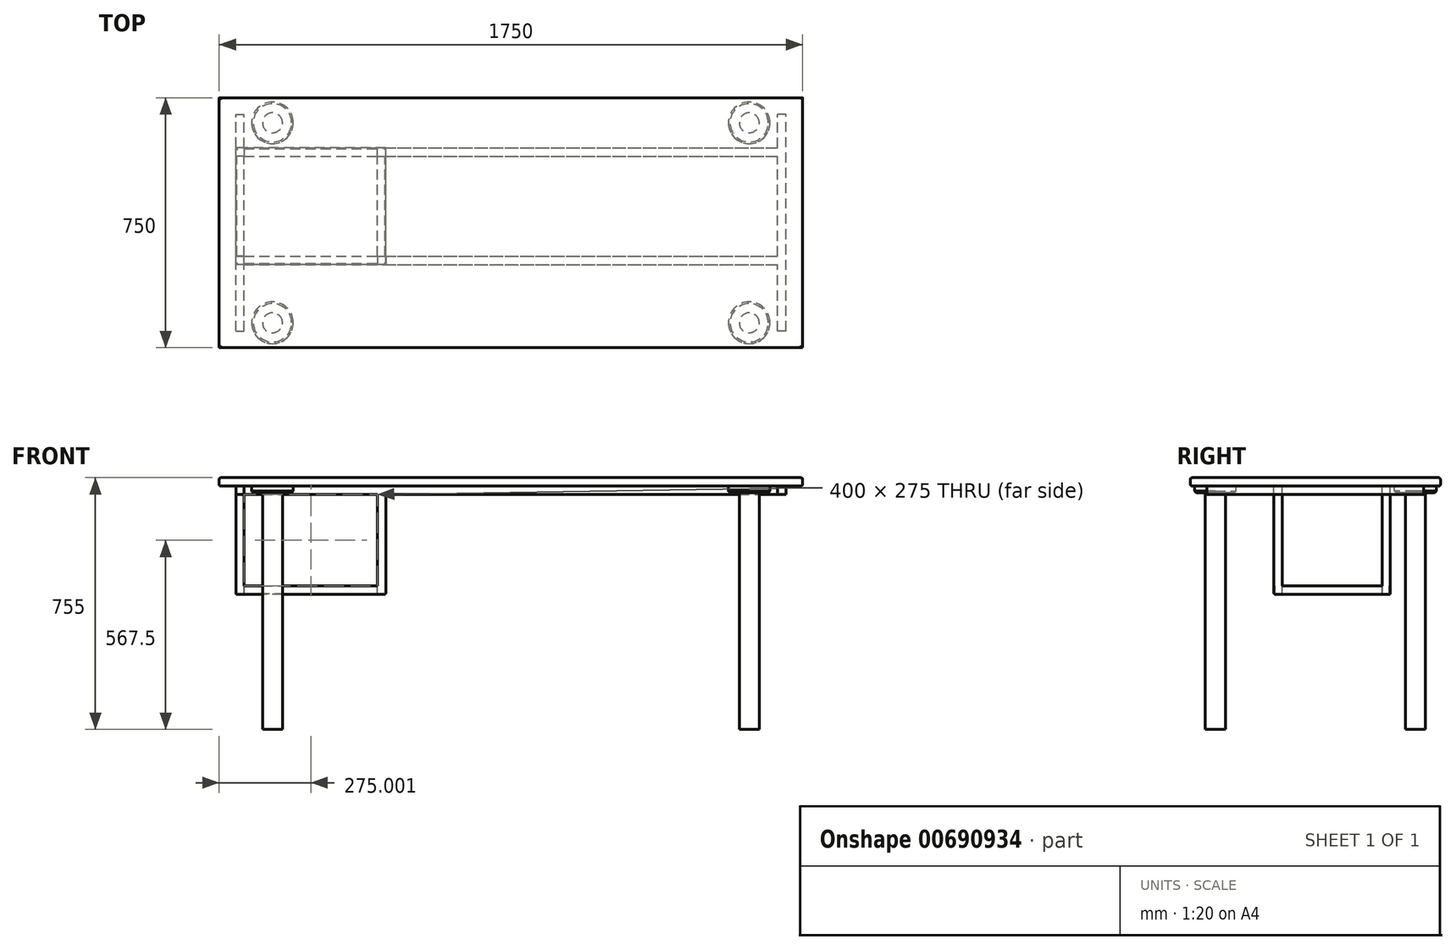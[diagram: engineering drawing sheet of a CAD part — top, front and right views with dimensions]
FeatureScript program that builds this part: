
annotation { "Feature Type Name" : "Feature", "Feature Type Description" : "" }
export const myFeature = defineFeature(function(context is Context, id is Id, definition is map)
    precondition{}
    {
        {
            var Q0;
            Q0=qCreatedBy(makeId("Top.planeOp"),FACE);
            var sketch = newSketch(context, id + "F0", { "sketchPlane" : qUnion([Q0])});
            skLineSegment(sketch, "E0.bottom", {"start": v(-773.1, 399.75) * mm, "end": v(976.9, 399.75) * mm});
            skLineSegment(sketch, "E0.top", {"start": v(-773.1, -350.25) * mm, "end": v(976.9, -350.25) * mm});
            skLineSegment(sketch, "E0.left", {"start": v(-773.1, 399.75) * mm, "end": v(-773.1, -350.25) * mm});
            skLineSegment(sketch, "E0.right", {"start": v(976.9, 399.75) * mm, "end": v(976.9, -350.25) * mm});
            skSolve(sketch);
        }
        {
            var Q0;
            Q0=makeQuery(id+"F0.imprint","IMPRINT",FACE,{"disambiguationData":[TD([[makeQuery(id+"F0.imprint","IMPRINT",EDGE,{"derivedFrom":sQuery(id+"F0.wireOp",EDGE,"E0.bottom")}),-1.0]])]});
            extrude(context, id + "F1", {"entities" : qUnion([Q0]), "depth" : 25 * mm, "offsetDistance" : 25 * mm});
        }
        {
            var Q0;
            Q0=makeQuery(id+"F1.opExtrude","CAP_FACE",FACE,{"disambiguationData":[OSD([sQuery(id+"F0.wireOp",EDGE,"E0.bottom"),sQuery(id+"F0.wireOp",EDGE,"E0.top"),sQuery(id+"F0.wireOp",EDGE,"E0.left"),sQuery(id+"F0.wireOp",EDGE,"E0.right")])],"isStart":true});
            var sketch = newSketch(context, id + "F2", { "sketchPlane" : qUnion([Q0])});
            skLineSegment(sketch, "E1.bottom", {"start": v(-723.1, 300.25) * mm, "end": v(-698.1, 300.25) * mm});
            skLineSegment(sketch, "E1.top", {"start": v(-723.1, -349.75) * mm, "end": v(-698.1, -349.75) * mm});
            skLineSegment(sketch, "E1.left", {"start": v(-723.1, 300.25) * mm, "end": v(-723.1, -349.75) * mm});
            skPoint(sketch, "E1.middle", {"position": v(-710.6, -24.75) * mm});
            skPoint(sketch, "E1.middle.positionSnap0", {"position": v(-773.1, -24.75) * mm});
            skPoint(sketch, "E1.centerSnap0", {"position": v(-773.1, -24.75) * mm});
            skLineSegment(sketch, "E2", {"start": v(101.9, 350.25) * mm, "end": v(101.9, -399.75) * mm, "construction": true});
            skLineSegment(sketch, "E3.MirrorCS", {"start": v(926.9, 300.25) * mm, "end": v(901.9, 300.25) * mm});
            skLineSegment(sketch, "E4.MirrorCS", {"start": v(926.9, 300.25) * mm, "end": v(926.9, -349.75) * mm});
            skLineSegment(sketch, "E5.MirrorCS", {"start": v(926.9, -349.75) * mm, "end": v(901.9, -349.75) * mm});
            skLineSegment(sketch, "E6.left", {"start": v(-723.1, -349.75) * mm, "end": v(-723.1, -324.75) * mm});
            skLineSegment(sketch, "E6.right", {"start": v(926.9, -349.75) * mm, "end": v(926.9, -324.75) * mm});
            skPoint(sketch, "E7.middle", {"position": v(101.9, -24.75) * mm});
            skPoint(sketch, "E8.orphan", {"position": v(901.9, -349.75) * mm});
            skLineSegment(sketch, "E9.trimOffspring", {"start": v(901.9, -349.75) * mm, "end": v(926.9, -349.75) * mm});
            skPoint(sketch, "E10.trimOffspring.start.orphan", {"position": v(-698.1, -37.25) * mm});
            skPoint(sketch, "E1.right.end.orphan", {"position": v(-698.1, -12.25) * mm});
            skPoint(sketch, "E11.MirrorCS.end.orphan", {"position": v(901.9, -12.25) * mm});
            skPoint(sketch, "E11.MirrorCS.start.orphan", {"position": v(901.9, 300.25) * mm});
            skPoint(sketch, "E12.trimOffspring.start.orphan", {"position": v(901.9, -37.25) * mm});
            skLineSegment(sketch, "E13", {"start": v(901.9, 300.25) * mm, "end": v(901.9, 100.25) * mm});
            skLineSegment(sketch, "E14", {"start": v(-698.1, 300.25) * mm, "end": v(-698.1, 100.25) * mm});
            skLineSegment(sketch, "E15.bottom", {"start": v(-698.1, -249.75) * mm, "end": v(901.9, -249.75) * mm});
            skLineSegment(sketch, "E15.top", {"start": v(-698.1, -224.75) * mm, "end": v(901.9, -224.75) * mm});
            skLineSegment(sketch, "E16.bottom", {"start": v(-698.1, 75.25) * mm, "end": v(901.9, 75.25) * mm});
            skLineSegment(sketch, "E16.top", {"start": v(-698.1, 100.25) * mm, "end": v(901.9, 100.25) * mm});
            skLineSegment(sketch, "E17.trimOffspring", {"start": v(-698.1, 75.25) * mm, "end": v(-698.1, -224.75) * mm});
            skLineSegment(sketch, "E18.trimOffspring", {"start": v(-698.1, -249.75) * mm, "end": v(-698.1, -349.75) * mm});
            skLineSegment(sketch, "E19.trimOffspring", {"start": v(901.9, -249.75) * mm, "end": v(901.9, -349.75) * mm});
            skLineSegment(sketch, "E20.trimOffspring", {"start": v(901.9, 75.25) * mm, "end": v(901.9, -224.75) * mm});
            skSolve(sketch);
        }
        {
            var Q0;
            Q0=makeQuery(id+"F2.imprint","IMPRINT",FACE,{"disambiguationData":[TD([[makeQuery(id+"F2.imprint","IMPRINT",EDGE,{"derivedFrom":sQuery(id+"F2.wireOp",EDGE,"E1.bottom")}),-1.0]])]});
            extrude(context, id + "F3", {"entities" : qUnion([Q0]), "operationType" : NewBodyOperationType.ADD, "depth" : 25 * mm, "offsetDistance" : 25 * mm});
        }
        {
            var Q0;
            {var subQ0=sQuery(id+"F0.wireOp",EDGE,"E0.left");var subQ1=sQuery(id+"F0.wireOp",EDGE,"E0.bottom");var subQ2=sQuery(id+"F0.wireOp",EDGE,"E0.right");var subQ3=sQuery(id+"F0.wireOp",EDGE,"E0.top");Q0=makeQuery(id+"F3.boolean.opBoolean","SPLIT",FACE,{"disambiguationData":[TD([makeQuery(id+"F1.opExtrude","SWEPT_FACE",FACE,{"disambiguationData":[OSD([subQ1])]})])],"derivedFrom":makeQuery(id+"F1.opExtrude","CAP_FACE",FACE,{"disambiguationData":[OSD([subQ1,subQ3,subQ0,subQ2])],"isStart":true})});}
            var sketch = newSketch(context, id + "F4", { "sketchPlane" : qUnion([Q0])});
            skLineSegment(sketch, "E21", {"start": v(-572.48, -324.75) * mm, "end": v(-698.1, -324.75) * mm, "construction": true});
            skLineSegment(sketch, "E22", {"start": v(-572.48, -324.75) * mm, "end": v(901.9, -324.75) * mm, "construction": true});
            skCircle(sketch, "E23", {"center": v(-613.1, -324.75) * mm, "radius": 62.5 * mm});
            skLineSegment(sketch, "E24", {"start": v(101.9, 350.25) * mm, "end": v(101.9, -399.75) * mm, "construction": true});
            skCircle(sketch, "E25", {"center": v(816.9, -324.75) * mm, "radius": 62.5 * mm});
            skCircle(sketch, "E26", {"center": v(-613.1, 275.25) * mm, "radius": 62.5 * mm});
            skCircle(sketch, "E27", {"center": v(816.9, 275.25) * mm, "radius": 62.5 * mm});
            skCircle(sketch, "E28", {"center": v(-613.1, 275.25) * mm, "radius": 30 * mm});
            skCircle(sketch, "E29", {"center": v(-613.1, -324.75) * mm, "radius": 30 * mm});
            skCircle(sketch, "E30", {"center": v(816.9, -324.75) * mm, "radius": 30 * mm});
            skCircle(sketch, "E31", {"center": v(816.9, 275.25) * mm, "radius": 30 * mm});
            skSolve(sketch);
        }
        {
            var Q0;
            Q0=makeQuery(id+"F4.imprint","IMPRINT",FACE,{"disambiguationData":[TD([[makeQuery(id+"F4.imprint","IMPRINT",EDGE,{"derivedFrom":sQuery(id+"F4.wireOp",EDGE,"E27")}),1.0]])]});
            var Q1;
            Q1=makeQuery(id+"F4.imprint","IMPRINT",FACE,{"disambiguationData":[TD([[makeQuery(id+"F4.imprint","IMPRINT",EDGE,{"derivedFrom":sQuery(id+"F4.wireOp",EDGE,"E26")}),1.0]])]});
            var Q2;
            Q2=makeQuery(id+"F4.imprint","IMPRINT",FACE,{"disambiguationData":[TD([[makeQuery(id+"F4.imprint","IMPRINT",EDGE,{"derivedFrom":sQuery(id+"F4.wireOp",EDGE,"E23")}),1.0]])]});
            var Q3;
            Q3=makeQuery(id+"F4.imprint","IMPRINT",FACE,{"disambiguationData":[TD([[makeQuery(id+"F4.imprint","IMPRINT",EDGE,{"derivedFrom":sQuery(id+"F4.wireOp",EDGE,"E25")}),1.0]])]});
            extrude(context, id + "F5", {"entities" : qUnion([Q0, Q1, Q2, Q3]), "operationType" : NewBodyOperationType.ADD, "depth" : 20 * mm, "offsetDistance" : 25 * mm});
        }
        {
            var Q0;
            {var subQ0=sQuery(id+"F0.wireOp",EDGE,"E0.left");var subQ1=sQuery(id+"F0.wireOp",EDGE,"E0.bottom");var subQ2=sQuery(id+"F0.wireOp",EDGE,"E0.right");var subQ3=sQuery(id+"F0.wireOp",EDGE,"E0.top");Q0=makeQuery(id+"F5.boolean.opBoolean","SPLIT",FACE,{"disambiguationData":[TD([makeQuery(id+"F5.opExtrude","SWEPT_FACE",FACE,{"disambiguationData":[OSD([sQuery(id+"F4.wireOp",EDGE,"E30")])]})])],"derivedFrom":makeQuery(id+"F3.boolean.opBoolean","SPLIT",FACE,{"disambiguationData":[TD([makeQuery(id+"F1.opExtrude","SWEPT_FACE",FACE,{"disambiguationData":[OSD([subQ1])]})])],"derivedFrom":makeQuery(id+"F1.opExtrude","CAP_FACE",FACE,{"disambiguationData":[OSD([subQ1,subQ3,subQ0,subQ2])],"isStart":true})})});}
            var Q1;
            {var subQ0=sQuery(id+"F0.wireOp",EDGE,"E0.left");var subQ1=sQuery(id+"F0.wireOp",EDGE,"E0.bottom");var subQ2=sQuery(id+"F0.wireOp",EDGE,"E0.right");var subQ3=sQuery(id+"F0.wireOp",EDGE,"E0.top");Q1=makeQuery(id+"F5.boolean.opBoolean","SPLIT",FACE,{"disambiguationData":[TD([makeQuery(id+"F5.opExtrude","SWEPT_FACE",FACE,{"disambiguationData":[OSD([sQuery(id+"F4.wireOp",EDGE,"E29")])]})])],"derivedFrom":makeQuery(id+"F3.boolean.opBoolean","SPLIT",FACE,{"disambiguationData":[TD([makeQuery(id+"F1.opExtrude","SWEPT_FACE",FACE,{"disambiguationData":[OSD([subQ1])]})])],"derivedFrom":makeQuery(id+"F1.opExtrude","CAP_FACE",FACE,{"disambiguationData":[OSD([subQ1,subQ3,subQ0,subQ2])],"isStart":true})})});}
            var Q2;
            {var subQ0=sQuery(id+"F0.wireOp",EDGE,"E0.left");var subQ1=sQuery(id+"F0.wireOp",EDGE,"E0.bottom");var subQ2=sQuery(id+"F0.wireOp",EDGE,"E0.right");var subQ3=sQuery(id+"F0.wireOp",EDGE,"E0.top");Q2=makeQuery(id+"F5.boolean.opBoolean","SPLIT",FACE,{"disambiguationData":[TD([makeQuery(id+"F5.opExtrude","SWEPT_FACE",FACE,{"disambiguationData":[OSD([sQuery(id+"F4.wireOp",EDGE,"E28")])]})])],"derivedFrom":makeQuery(id+"F3.boolean.opBoolean","SPLIT",FACE,{"disambiguationData":[TD([makeQuery(id+"F1.opExtrude","SWEPT_FACE",FACE,{"disambiguationData":[OSD([subQ1])]})])],"derivedFrom":makeQuery(id+"F1.opExtrude","CAP_FACE",FACE,{"disambiguationData":[OSD([subQ1,subQ3,subQ0,subQ2])],"isStart":true})})});}
            var Q3;
            {var subQ0=sQuery(id+"F0.wireOp",EDGE,"E0.left");var subQ1=sQuery(id+"F0.wireOp",EDGE,"E0.bottom");var subQ2=sQuery(id+"F0.wireOp",EDGE,"E0.right");var subQ3=sQuery(id+"F0.wireOp",EDGE,"E0.top");Q3=makeQuery(id+"F5.boolean.opBoolean","SPLIT",FACE,{"disambiguationData":[TD([makeQuery(id+"F5.opExtrude","SWEPT_FACE",FACE,{"disambiguationData":[OSD([sQuery(id+"F4.wireOp",EDGE,"E31")])]})])],"derivedFrom":makeQuery(id+"F3.boolean.opBoolean","SPLIT",FACE,{"disambiguationData":[TD([makeQuery(id+"F1.opExtrude","SWEPT_FACE",FACE,{"disambiguationData":[OSD([subQ1])]})])],"derivedFrom":makeQuery(id+"F1.opExtrude","CAP_FACE",FACE,{"disambiguationData":[OSD([subQ1,subQ3,subQ0,subQ2])],"isStart":true})})});}
            extrude(context, id + "F6", {"entities" : qUnion([Q0, Q1, Q2, Q3]), "operationType" : NewBodyOperationType.ADD, "depth" : 730 * mm, "offsetDistance" : 25 * mm});
        }
        {
            var Q0;
            Q0=makeQuery(id+"F3.opExtrude","CAP_FACE",FACE,{"disambiguationData":[OSD([sQuery(id+"F2.wireOp",EDGE,"E1.bottom"),sQuery(id+"F2.wireOp",EDGE,"E1.left"),sQuery(id+"F2.wireOp",EDGE,"E3.MirrorCS"),sQuery(id+"F2.wireOp",EDGE,"E4.MirrorCS"),sQuery(id+"F2.wireOp",EDGE,"E1.top"),sQuery(id+"F2.wireOp",EDGE,"E6.left"),sQuery(id+"F2.wireOp",EDGE,"E6.right"),sQuery(id+"F2.wireOp",EDGE,"E9.trimOffspring"),sQuery(id+"F2.wireOp",EDGE,"E13"),sQuery(id+"F2.wireOp",EDGE,"E14"),sQuery(id+"F2.wireOp",EDGE,"E15.bottom"),sQuery(id+"F2.wireOp",EDGE,"E15.top"),sQuery(id+"F2.wireOp",EDGE,"E16.bottom"),sQuery(id+"F2.wireOp",EDGE,"E16.top"),sQuery(id+"F2.wireOp",EDGE,"E17.trimOffspring"),sQuery(id+"F2.wireOp",EDGE,"E18.trimOffspring"),sQuery(id+"F2.wireOp",EDGE,"E19.trimOffspring"),sQuery(id+"F2.wireOp",EDGE,"E20.trimOffspring")])],"isStart":false});
            var sketch = newSketch(context, id + "F7", { "sketchPlane" : qUnion([Q0])});
            skLineSegment(sketch, "E32.bottom", {"start": v(-698.1, 100.25) * mm, "end": v(-723.1, 100.25) * mm});
            skLineSegment(sketch, "E32.top", {"start": v(-698.1, 75.25) * mm, "end": v(-723.1, 75.25) * mm});
            skLineSegment(sketch, "E32.left", {"start": v(-698.1, 100.25) * mm, "end": v(-698.1, 75.25) * mm});
            skLineSegment(sketch, "E32.right", {"start": v(-723.1, 100.25) * mm, "end": v(-723.1, 75.25) * mm});
            skLineSegment(sketch, "E33.bottom", {"start": v(-698.1, -249.75) * mm, "end": v(-723.1, -249.75) * mm});
            skLineSegment(sketch, "E33.top", {"start": v(-698.1, -224.75) * mm, "end": v(-723.1, -224.75) * mm});
            skLineSegment(sketch, "E33.left", {"start": v(-698.1, -249.75) * mm, "end": v(-698.1, -224.75) * mm});
            skLineSegment(sketch, "E33.right", {"start": v(-723.1, -249.75) * mm, "end": v(-723.1, -224.75) * mm});
            skLineSegment(sketch, "E34.bottom", {"start": v(-298.1, -224.75) * mm, "end": v(-273.1, -224.75) * mm});
            skLineSegment(sketch, "E34.top", {"start": v(-298.1, -249.75) * mm, "end": v(-273.1, -249.75) * mm});
            skLineSegment(sketch, "E34.left", {"start": v(-298.1, -224.75) * mm, "end": v(-298.1, -249.75) * mm});
            skLineSegment(sketch, "E34.right", {"start": v(-273.1, -224.75) * mm, "end": v(-273.1, -249.75) * mm});
            skLineSegment(sketch, "E35.bottom", {"start": v(-273.1, 75.25) * mm, "end": v(-298.1, 75.25) * mm});
            skLineSegment(sketch, "E35.top", {"start": v(-273.1, 100.25) * mm, "end": v(-298.1, 100.25) * mm});
            skLineSegment(sketch, "E35.left", {"start": v(-273.1, 75.25) * mm, "end": v(-273.1, 100.25) * mm});
            skLineSegment(sketch, "E35.right", {"start": v(-298.1, 75.25) * mm, "end": v(-298.1, 100.25) * mm});
            skSolve(sketch);
        }
        {
            var Q0;
            Q0=makeQuery(id+"F7.imprint","IMPRINT",FACE,{"disambiguationData":[TD([[makeQuery(id+"F7.imprint","IMPRINT",EDGE,{"derivedFrom":sQuery(id+"F7.wireOp",EDGE,"E32.bottom")}),1.0]])]});
            var Q1;
            Q1=makeQuery(id+"F7.imprint","IMPRINT",FACE,{"disambiguationData":[TD([[makeQuery(id+"F7.imprint","IMPRINT",EDGE,{"derivedFrom":sQuery(id+"F7.wireOp",EDGE,"E35.bottom")}),1.0]])]});
            var Q2;
            Q2=makeQuery(id+"F7.imprint","IMPRINT",FACE,{"disambiguationData":[TD([[makeQuery(id+"F7.imprint","IMPRINT",EDGE,{"derivedFrom":sQuery(id+"F7.wireOp",EDGE,"E34.bottom")}),-1.0]])]});
            var Q3;
            Q3=makeQuery(id+"F7.imprint","IMPRINT",FACE,{"disambiguationData":[TD([[makeQuery(id+"F7.imprint","IMPRINT",EDGE,{"derivedFrom":sQuery(id+"F7.wireOp",EDGE,"E33.bottom")}),-1.0]])]});
            extrude(context, id + "F8", {"entities" : qUnion([Q0, Q1, Q2, Q3]), "operationType" : NewBodyOperationType.ADD, "depth" : 300 * mm, "offsetDistance" : 25 * mm});
        }
        {
            var Q0;
            Q0=makeQuery(id+"F8.boolean.opBoolean","MERGE",FACE,{"derivedFrom":[makeQuery(id+"F3.opExtrude","SWEPT_FACE",FACE,{"disambiguationData":[OSD([sQuery(id+"F2.wireOp",EDGE,"E15.top")])]}),makeQuery(id+"F8.opExtrude","SWEPT_FACE",FACE,{"disambiguationData":[OSD([sQuery(id+"F7.wireOp",EDGE,"E34.bottom")])]})]});
            var sketch = newSketch(context, id + "F9", { "sketchPlane" : qUnion([Q0])});
            skLineSegment(sketch, "E36.0", {"start": v(-723.1, -325) * mm, "end": v(-723.1, -25) * mm});
            skLineSegment(sketch, "E37.0", {"start": v(-698.1, -325) * mm, "end": v(-723.1, -325) * mm});
            skLineSegment(sketch, "E38.0", {"start": v(-298.1, -325) * mm, "end": v(-273.1, -325) * mm});
            skLineSegment(sketch, "E39.0", {"start": v(-273.1, -325) * mm, "end": v(-273.1, -25) * mm});
            skLineSegment(sketch, "E40.bottom", {"start": v(-723.1, -300) * mm, "end": v(-720.1, -300) * mm});
            skLineSegment(sketch, "E40.top", {"start": v(-723.1, -325) * mm, "end": v(-720.1, -325) * mm});
            skLineSegment(sketch, "E40.left", {"start": v(-723.1, -300) * mm, "end": v(-723.1, -325) * mm});
            skLineSegment(sketch, "E40.right", {"start": v(-720.1, -300) * mm, "end": v(-720.1, -322) * mm});
            skLineSegment(sketch, "E41.bottom", {"start": v(-698.1, -325) * mm, "end": v(-719.87, -325) * mm});
            skLineSegment(sketch, "E41.top", {"start": v(-698.1, -322) * mm, "end": v(-720.1, -322) * mm});
            skLineSegment(sketch, "E41.left", {"start": v(-698.1, -325) * mm, "end": v(-698.1, -322) * mm});
            skLineSegment(sketch, "E42", {"start": v(-698.1, -325) * mm, "end": v(-298.1, -325) * mm, "construction": true});
            skLineSegment(sketch, "E43", {"start": v(-498.1, -325) * mm, "end": v(-498.1, -169.42) * mm, "construction": true});
            skLineSegment(sketch, "E44.MirrorCS", {"start": v(-298.1, -322) * mm, "end": v(-276.1, -322) * mm});
            skLineSegment(sketch, "E45.MirrorCS", {"start": v(-298.1, -325) * mm, "end": v(-298.1, -322) * mm});
            skLineSegment(sketch, "E46.MirrorCS", {"start": v(-273.1, -300) * mm, "end": v(-276.1, -300) * mm});
            skLineSegment(sketch, "E47.MirrorCS", {"start": v(-276.1, -300) * mm, "end": v(-276.1, -322) * mm});
            skSolve(sketch);
        }
        {
            var Q0;
            Q0=makeQuery(id+"F9.imprint","IMPRINT",FACE,{"disambiguationData":[TD([[makeQuery(id+"F9.imprint","IMPRINT",EDGE,{"derivedFrom":sQuery(id+"F9.wireOp",EDGE,"E37.0")}),-1.0]])]});
            var Q1;
            Q1=makeQuery(id+"F9.imprint","IMPRINT",FACE,{"disambiguationData":[TD([[makeQuery(id+"F9.imprint","IMPRINT",EDGE,{"derivedFrom":sQuery(id+"F9.wireOp",EDGE,"E44.MirrorCS")}),-1.0]])]});
            extrude(context, id + "F10", {"entities" : qUnion([Q0, Q1]), "operationType" : NewBodyOperationType.ADD, "endBound" : BoundingType.UP_TO_NEXT, "depth" : 25 * mm, "offsetDistance" : 25 * mm});
        }
        {
            var Q0;
            Q0=makeQuery(id+"F10.boolean.opBoolean","MERGE",FACE,{"derivedFrom":[makeQuery(id+"F8.opExtrude","SWEPT_FACE",FACE,{"disambiguationData":[OSD([sQuery(id+"F7.wireOp",EDGE,"E34.left")])]}),makeQuery(id+"F8.opExtrude","SWEPT_FACE",FACE,{"disambiguationData":[OSD([sQuery(id+"F7.wireOp",EDGE,"E35.right")])]}),makeQuery(id+"F10.opExtrude","SWEPT_FACE",FACE,{"disambiguationData":[OSD([sQuery(id+"F9.wireOp",EDGE,"E45.MirrorCS")])]})]});
            var sketch = newSketch(context, id + "F11", { "sketchPlane" : qUnion([Q0])});
            skLineSegment(sketch, "E48.bottom", {"start": v(-224.75, -322) * mm, "end": v(-246.75, -322) * mm});
            skLineSegment(sketch, "E48.top", {"start": v(-224.75, -325) * mm, "end": v(-249.75, -325) * mm});
            skLineSegment(sketch, "E48.left", {"start": v(-224.75, -322) * mm, "end": v(-224.75, -325) * mm});
            skLineSegment(sketch, "E48.right", {"start": v(-249.75, -322) * mm, "end": v(-249.75, -325) * mm});
            skLineSegment(sketch, "E49.top", {"start": v(-249.75, -300) * mm, "end": v(-246.75, -300) * mm});
            skLineSegment(sketch, "E49.left", {"start": v(-249.75, -322) * mm, "end": v(-249.75, -300) * mm});
            skLineSegment(sketch, "E49.right", {"start": v(-246.75, -322) * mm, "end": v(-246.75, -300) * mm});
            skLineSegment(sketch, "E50", {"start": v(-74.75, -322) * mm, "end": v(-74.75, -216.9) * mm, "construction": true});
            skLineSegment(sketch, "E51.MirrorCS", {"start": v(75.25, -322) * mm, "end": v(97.25, -322) * mm});
            skLineSegment(sketch, "E52.MirrorCS", {"start": v(75.25, -322) * mm, "end": v(75.25, -325) * mm});
            skLineSegment(sketch, "E53.MirrorCS", {"start": v(75.25, -325) * mm, "end": v(100.25, -325) * mm});
            skLineSegment(sketch, "E54.MirrorCS", {"start": v(100.25, -322) * mm, "end": v(100.25, -300) * mm});
            skLineSegment(sketch, "E55.MirrorCS", {"start": v(100.25, -322) * mm, "end": v(100.25, -325) * mm});
            skLineSegment(sketch, "E56.MirrorCS", {"start": v(97.25, -322) * mm, "end": v(97.25, -300) * mm});
            skLineSegment(sketch, "E57.MirrorCS", {"start": v(100.25, -300) * mm, "end": v(97.25, -300) * mm});
            skSolve(sketch);
        }
        {
            var Q0;
            Q0=makeQuery(id+"F11.imprint","IMPRINT",FACE,{"disambiguationData":[TD([[makeQuery(id+"F11.imprint","IMPRINT",EDGE,{"derivedFrom":sQuery(id+"F11.wireOp",EDGE,"E48.bottom")}),1.0]])]});
            var Q1;
            Q1=makeQuery(id+"F11.imprint","IMPRINT",FACE,{"disambiguationData":[TD([[makeQuery(id+"F11.imprint","IMPRINT",EDGE,{"derivedFrom":sQuery(id+"F11.wireOp",EDGE,"E51.MirrorCS")}),-1.0]])]});
            extrude(context, id + "F12", {"entities" : qUnion([Q0, Q1]), "operationType" : NewBodyOperationType.ADD, "endBound" : BoundingType.UP_TO_NEXT, "depth" : 25 * mm, "offsetDistance" : 25 * mm});
        }
        {
            var Q0;
            {var subQ0=sQuery(id+"F7.wireOp",EDGE,"E32.right");Q0=makeQuery(id+"F10.boolean.opBoolean","MERGE",EDGE,{"derivedFrom":[makeQuery(id+"F8.opExtrude","CAP_EDGE",EDGE,{"disambiguationData":[OSD([subQ0])],"isStart":false}),makeQuery(id+"F8.opExtrude","CAP_EDGE",EDGE,{"disambiguationData":[OSD([sQuery(id+"F7.wireOp",EDGE,"E33.right")])],"isStart":false}),makeQuery(id+"F10.opExtrude","SWEPT_EDGE",EDGE,{"disambiguationData":[OSD([sQuery(id+"F2.wireOp",EDGE,"E1.left"),sQuery(id+"F2.wireOp",EDGE,"E6.left"),sQuery(id+"F7.wireOp",EDGE,"E32.top"),subQ0])]})]});}
            var Q1;
            Q1=makeQuery(id+"F12.boolean.opBoolean","MERGE",EDGE,{"derivedFrom":[makeQuery(id+"F8.opExtrude","CAP_EDGE",EDGE,{"disambiguationData":[OSD([sQuery(id+"F7.wireOp",EDGE,"E32.bottom")])],"isStart":false}),makeQuery(id+"F8.opExtrude","CAP_EDGE",EDGE,{"disambiguationData":[OSD([sQuery(id+"F7.wireOp",EDGE,"E35.top")])],"isStart":false}),makeQuery(id+"F12.opExtrude","SWEPT_EDGE",EDGE,{"disambiguationData":[OSD([sQuery(id+"F11.wireOp",EDGE,"E53.MirrorCS"),sQuery(id+"F11.wireOp",EDGE,"E55.MirrorCS")])]})]});
            var Q2;
            Q2=makeQuery(id+"F10.boolean.opBoolean","MERGE",EDGE,{"derivedFrom":[makeQuery(id+"F8.opExtrude","CAP_EDGE",EDGE,{"disambiguationData":[OSD([sQuery(id+"F7.wireOp",EDGE,"E34.right")])],"isStart":false}),makeQuery(id+"F8.opExtrude","CAP_EDGE",EDGE,{"disambiguationData":[OSD([sQuery(id+"F7.wireOp",EDGE,"E35.left")])],"isStart":false}),makeQuery(id+"F10.opExtrude","SWEPT_EDGE",EDGE,{"disambiguationData":[OSD([sQuery(id+"F9.wireOp",EDGE,"E38.0"),sQuery(id+"F9.wireOp",EDGE,"E39.0")])]})]});
            var Q3;
            Q3=makeQuery(id+"F12.boolean.opBoolean","MERGE",EDGE,{"derivedFrom":[makeQuery(id+"F8.opExtrude","CAP_EDGE",EDGE,{"disambiguationData":[OSD([sQuery(id+"F7.wireOp",EDGE,"E33.bottom")])],"isStart":false}),makeQuery(id+"F8.opExtrude","CAP_EDGE",EDGE,{"disambiguationData":[OSD([sQuery(id+"F7.wireOp",EDGE,"E34.top")])],"isStart":false}),makeQuery(id+"F12.opExtrude","SWEPT_EDGE",EDGE,{"disambiguationData":[OSD([sQuery(id+"F11.wireOp",EDGE,"E48.top"),sQuery(id+"F11.wireOp",EDGE,"E48.right")])]})]});
            fillet(context, id + "F13", {"entities" : qUnion([Q0, Q1, Q2, Q3]), "radius" : 5 * mm, "tangentPropagation" : true, "allowEdgeOverflow" : false});
        }
        {
            var Q0;
            Q0=makeQuery(id+"F1.opExtrude","CAP_FACE",FACE,{"disambiguationData":[OSD([sQuery(id+"F0.wireOp",EDGE,"E0.bottom"),sQuery(id+"F0.wireOp",EDGE,"E0.top"),sQuery(id+"F0.wireOp",EDGE,"E0.left"),sQuery(id+"F0.wireOp",EDGE,"E0.right")])],"isStart":false});
            var Q1;
            Q1=makeQuery(id+"F1.opExtrude","CAP_EDGE",EDGE,{"disambiguationData":[OSD([sQuery(id+"F0.wireOp",EDGE,"E0.top")])],"isStart":true});
            var Q2;
            Q2=makeQuery(id+"F1.opExtrude","CAP_EDGE",EDGE,{"disambiguationData":[OSD([sQuery(id+"F0.wireOp",EDGE,"E0.left")])],"isStart":true});
            var Q3;
            Q3=makeQuery(id+"F1.opExtrude","CAP_EDGE",EDGE,{"disambiguationData":[OSD([sQuery(id+"F0.wireOp",EDGE,"E0.right")])],"isStart":true});
            var Q4;
            Q4=makeQuery(id+"F1.opExtrude","CAP_EDGE",EDGE,{"disambiguationData":[OSD([sQuery(id+"F0.wireOp",EDGE,"E0.bottom")])],"isStart":true});
            fillet(context, id + "F14", {"entities" : qUnion([Q0, Q1, Q2, Q3, Q4]), "radius" : 5 * mm, "tangentPropagation" : true, "allowEdgeOverflow" : false});
        }
        {
            var Q0;
            Q0=makeQuery(id+"F5.opExtrude","CAP_EDGE",EDGE,{"disambiguationData":[OSD([sQuery(id+"F4.wireOp",EDGE,"E26")])],"isStart":false});
            var Q1;
            Q1=makeQuery(id+"F5.opExtrude","CAP_EDGE",EDGE,{"disambiguationData":[OSD([sQuery(id+"F4.wireOp",EDGE,"E27")])],"isStart":false});
            var Q2;
            Q2=makeQuery(id+"F5.opExtrude","CAP_EDGE",EDGE,{"disambiguationData":[OSD([sQuery(id+"F4.wireOp",EDGE,"E25")])],"isStart":false});
            var Q3;
            Q3=makeQuery(id+"F5.opExtrude","CAP_EDGE",EDGE,{"disambiguationData":[OSD([sQuery(id+"F4.wireOp",EDGE,"E23")])],"isStart":false});
            chamfer(context, id + "F15", {"entities" : qUnion([Q0, Q1, Q2, Q3]), "width" : 5 * mm, "tangentPropagation" : true});
        }
    });
